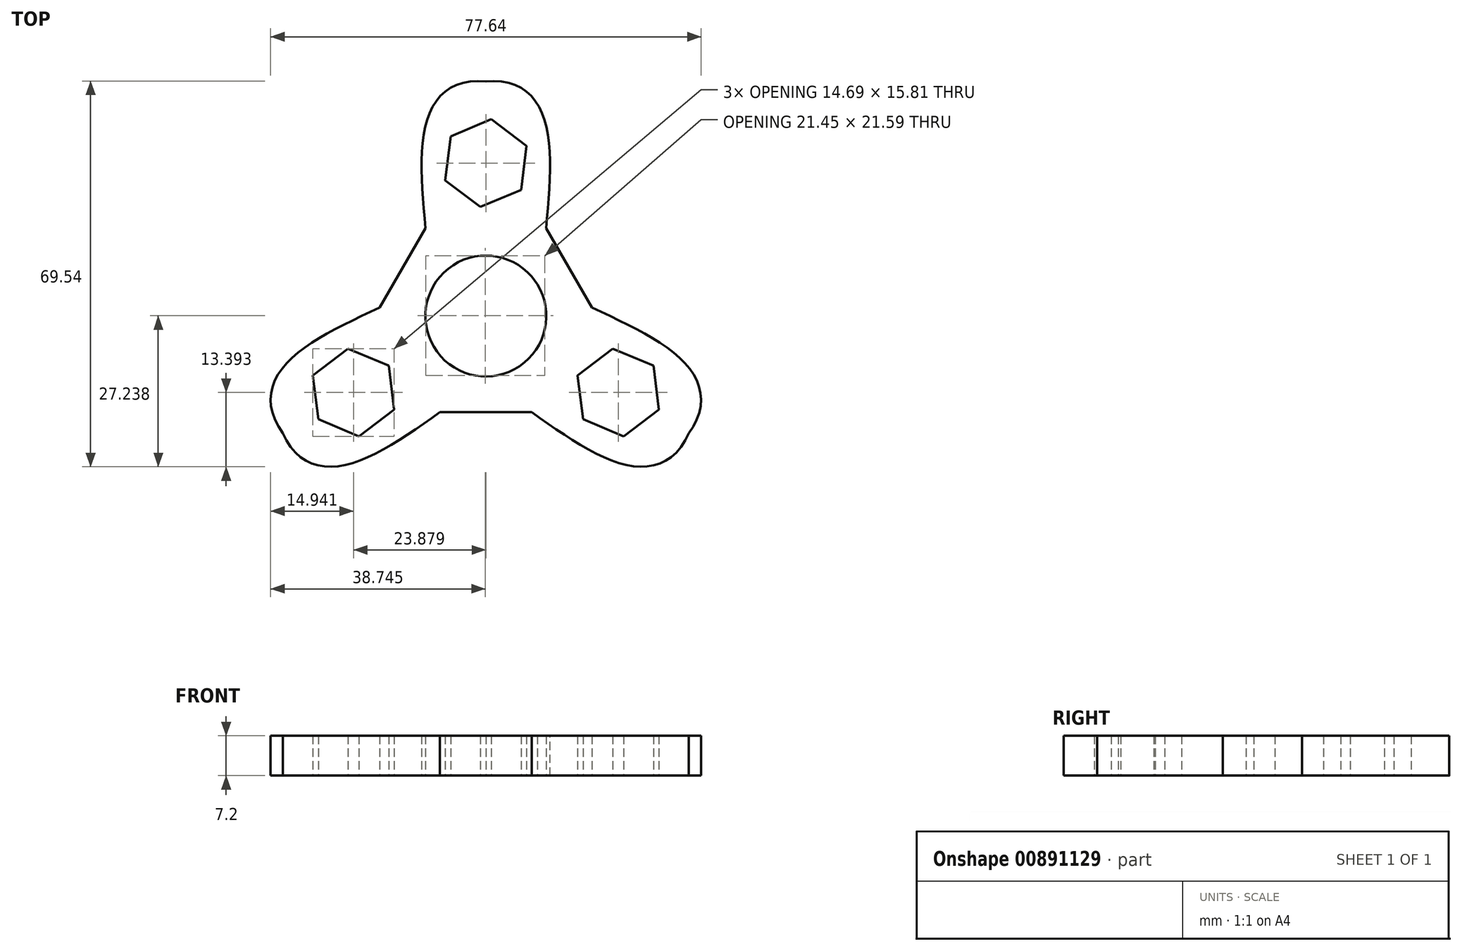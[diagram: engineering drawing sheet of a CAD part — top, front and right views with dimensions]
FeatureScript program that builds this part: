
annotation { "Feature Type Name" : "Feature", "Feature Type Description" : "" }
export const myFeature = defineFeature(function(context is Context, id is Id, definition is map)
    precondition{}
    {
        {
            var Q0;
            Q0=qCreatedBy(makeId("Top.planeOp"),FACE);
            var sketch = newSketch(context, id + "F0", { "sketchPlane" : qUnion([Q0])});
            skArc(sketch, "E0", {"start": v(8.27, 7.1) * mm, "mid": v(-8.8, -6.43) * mm, "end": v(9.28, 5.71) * mm});
            skLineSegment(sketch, "E1", {"start": v(16.98, -9.8) * mm, "end": v(17.4, -10.04) * mm});
            skLineSegment(sketch, "E2", {"start": v(0, 19.6) * mm, "end": v(0, 20.09) * mm});
            skCircle(sketch, "E3.cCircle", {"center": v(0, 27.57) * mm, "radius": 7.97 * mm, "construction": true});
            skLineSegment(sketch, "E3.0", {"start": v(1, 35.48) * mm, "end": v(7.34, 30.67) * mm});
            skLineSegment(sketch, "E3.1", {"start": v(7.34, 30.67) * mm, "end": v(6.35, 22.76) * mm});
            skLineSegment(sketch, "E3.2", {"start": v(6.35, 22.76) * mm, "end": v(-1, 19.67) * mm});
            skLineSegment(sketch, "E3.3", {"start": v(-1, 19.67) * mm, "end": v(-7.34, 24.48) * mm});
            skLineSegment(sketch, "E3.4", {"start": v(-7.34, 24.48) * mm, "end": v(-6.35, 32.39) * mm});
            skLineSegment(sketch, "E3.5", {"start": v(-6.35, 32.39) * mm, "end": v(1, 35.48) * mm});
            skCircle(sketch, "E4.MirrorC", {"center": v(-23.88, -13.79) * mm, "radius": 7.97 * mm, "construction": true});
            skLineSegment(sketch, "E5.MirrorCS", {"start": v(-24.87, -5.88) * mm, "end": v(-31.22, -10.7) * mm});
            skLineSegment(sketch, "E6.MirrorCS", {"start": v(-17.53, -8.97) * mm, "end": v(-24.87, -5.88) * mm});
            skLineSegment(sketch, "E7.MirrorCS", {"start": v(-16.54, -16.88) * mm, "end": v(-17.53, -8.97) * mm});
            skLineSegment(sketch, "E8.MirrorCS", {"start": v(-30.23, -18.6) * mm, "end": v(-22.89, -21.7) * mm});
            skLineSegment(sketch, "E9.MirrorCS", {"start": v(-22.89, -21.7) * mm, "end": v(-16.54, -16.88) * mm});
            skLineSegment(sketch, "E10.MirrorCS", {"start": v(-31.22, -10.7) * mm, "end": v(-30.23, -18.6) * mm});
            skCircle(sketch, "E11.MirrorC", {"center": v(23.88, -13.79) * mm, "radius": 7.97 * mm, "construction": true});
            skLineSegment(sketch, "E12.MirrorCS", {"start": v(17.53, -18.6) * mm, "end": v(24.87, -21.7) * mm});
            skLineSegment(sketch, "E13.MirrorCS", {"start": v(22.89, -5.88) * mm, "end": v(16.54, -10.7) * mm});
            skLineSegment(sketch, "E14.MirrorCS", {"start": v(24.87, -21.7) * mm, "end": v(31.22, -16.88) * mm});
            skLineSegment(sketch, "E15.MirrorCS", {"start": v(31.22, -16.88) * mm, "end": v(30.23, -8.97) * mm});
            skLineSegment(sketch, "E16.MirrorCS", {"start": v(16.54, -10.7) * mm, "end": v(17.53, -18.6) * mm});
            skLineSegment(sketch, "E17.MirrorCS", {"start": v(30.23, -8.97) * mm, "end": v(22.89, -5.88) * mm});
            skPoint(sketch, "E18.2.internal.orphan", {"position": v(0, 40.27) * mm});
            skFitSpline(sketch, "E19", {"points": [v(17.53, 0) * mm, v(37.07, -11.27) * mm, v(34.37, -24.57) * mm, v(24.94, -26.76) * mm, v(8.27, -17.33) * mm], "startDerivative": vector(85.76, -28.7) * mm, "endDerivative": vector(-63, 44.53) * mm});
            skLineSegment(sketch, "E20", {"start": v(30.36, -17.53) * mm, "end": v(30.78, -17.77) * mm});
            skPoint(sketch, "E21.3.internal.orphan", {"position": v(5.9, 40.27) * mm});
            skPoint(sketch, "E22.0.internal.orphan", {"position": v(-6.72, -16.88) * mm});
            skPoint(sketch, "E22.5.internal.orphan", {"position": v(-22.22, 0) * mm});
            skFitSpline(sketch, "E23.MirrorCS", {"points": [v(8.77, -15.18) * mm, v(28.3, -26.47) * mm, v(38.47, -17.48) * mm, v(35.65, -8.22) * mm, v(19.14, 1.5) * mm], "startDerivative": vector(67.74, -59.92) * mm, "endDerivative": vector(-70.07, 32.3) * mm});
            skFitSpline(sketch, "E24.MirrorCS", {"points": [v(-8.77, -15.18) * mm, v(-28.3, -26.47) * mm, v(-38.47, -17.48) * mm, v(-35.65, -8.22) * mm, v(-19.14, 1.5) * mm], "startDerivative": vector(-67.74, -59.92) * mm, "endDerivative": vector(70.07, 32.3) * mm});
            skFitSpline(sketch, "E25.MirrorCS", {"points": [v(-17.53, 0) * mm, v(-37.07, -11.27) * mm, v(-34.37, -24.57) * mm, v(-24.94, -26.76) * mm, v(-8.27, -17.33) * mm], "startDerivative": vector(-85.76, -28.7) * mm, "endDerivative": vector(63, 44.53) * mm});
            skFitSpline(sketch, "E26.MirrorCS", {"points": [v(-8.77, 15.18) * mm, v(-8.78, 37.74) * mm, v(4.1, 42.06) * mm, v(10.7, 34.98) * mm, v(10.88, 15.82) * mm], "startDerivative": vector(-18.02, 88.63) * mm, "endDerivative": vector(-7.07, -76.82) * mm});
            skFitSpline(sketch, "E27.MirrorCS", {"points": [v(8.77, 15.18) * mm, v(8.78, 37.74) * mm, v(-4.1, 42.06) * mm, v(-10.7, 34.98) * mm, v(-10.88, 15.82) * mm], "startDerivative": vector(18.02, 88.63) * mm, "endDerivative": vector(7.07, -76.82) * mm});
            skLineSegment(sketch, "E28.trimOffspring", {"start": v(-16.98, -9.8) * mm, "end": v(-17.4, -10.04) * mm});
            skPoint(sketch, "E29.1.internal.orphan", {"position": v(8.27, 7.1) * mm});
            skFitSpline(sketch, "E30", {"points": [v(8.27, 7.1) * mm, v(9.28, 5.71) * mm], "startDerivative": vector(1.02, -1.39) * mm, "endDerivative": vector(1.02, -1.39) * mm});
            skPoint(sketch, "E31.1.internal.orphan", {"position": v(0, -10.9) * mm});
            skLineSegment(sketch, "E32", {"start": v(-10.88, 15.82) * mm, "end": v(-19.14, 1.5) * mm});
            skLineSegment(sketch, "E33", {"start": v(10.88, 15.82) * mm, "end": v(19.14, 1.5) * mm});
            skLineSegment(sketch, "E34", {"start": v(8.27, -17.33) * mm, "end": v(-8.27, -17.33) * mm});
            skLineSegment(sketch, "E35", {"start": v(0.06, -10.9) * mm, "end": v(0.1, -17.33) * mm});
            skPoint(sketch, "E36.orphan", {"position": v(1, -169.19) * mm});
            skSolve(sketch);
        }
        {
            var Q0;
            Q0=makeQuery(id+"F0.imprint","IMPRINT",FACE,{"disambiguationData":[TD([[makeQuery(id+"F0.imprint","IMPRINT",EDGE,{"derivedFrom":sQuery(id+"F0.wireOp",EDGE,"E3.0")}),1.0]])]});
            extrude(context, id + "F1", {"entities" : qUnion([Q0]), "depth" : 7.2 * mm, "offsetDistance" : 25 * mm});
        }
    });
